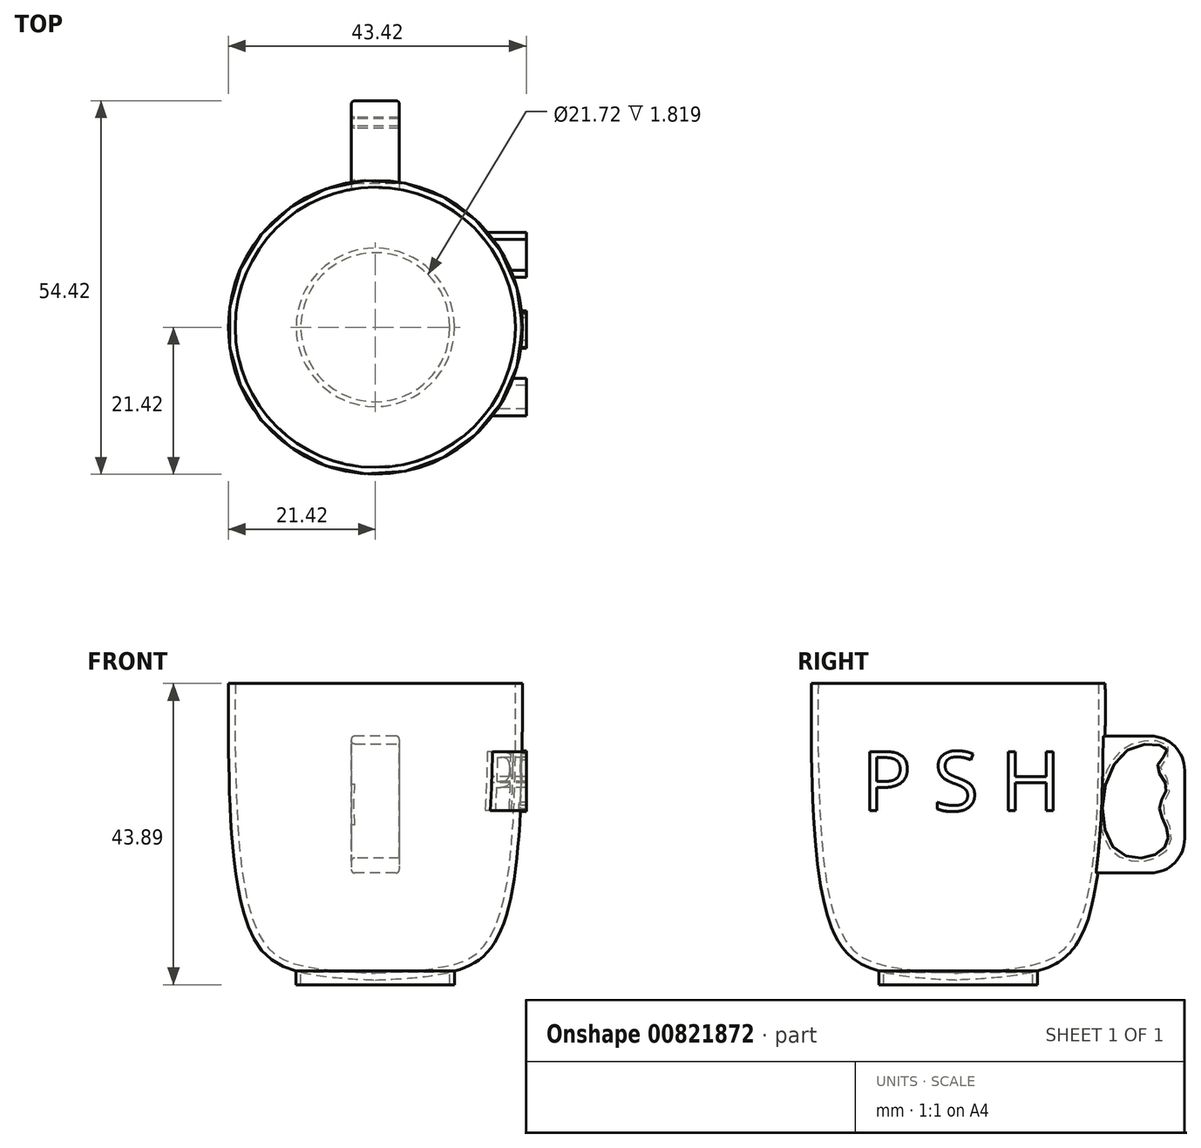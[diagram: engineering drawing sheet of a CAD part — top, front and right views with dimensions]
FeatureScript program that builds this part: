
annotation { "Feature Type Name" : "Feature", "Feature Type Description" : "" }
export const myFeature = defineFeature(function(context is Context, id is Id, definition is map)
    precondition{}
    {
        {
            var Q0;
            Q0=qCreatedBy(makeId("Front.planeOp"),FACE);
            var sketch = newSketch(context, id + "F0", { "sketchPlane" : qUnion([Q0])});
            skFitSpline(sketch, "E0", {"points": [v(-1.95, -31.25) * mm, v(9.5, -30.33) * mm, v(17.51, -25.53) * mm, v(21.4, 15) * mm], "startDerivative": vector(44.83, 1.61) * mm, "endDerivative": vector(-0.44, 101.6) * mm});
            skFitSpline(sketch, "E1.0", {"points": [v(-1.98, -30.25) * mm, v(-1.05, -30.22) * mm, v(0.82, -30.15) * mm, v(3.56, -30) * mm, v(6.23, -29.8) * mm, v(8.36, -29.52) * mm, v(10, -29.23) * mm, v(11.54, -28.88) * mm, v(13.3, -28.26) * mm, v(14.8, -27.29) * mm, v(15.87, -26.18) * mm, v(16.6, -25.15) * mm, v(17.27, -23.88) * mm, v(18.06, -21.85) * mm, v(18.87, -18.74) * mm, v(19.57, -14.26) * mm, v(20.03, -9.15) * mm, v(20.3, -3.55) * mm, v(20.45, 4.41) * mm, v(20.42, 10.76) * mm, v(20.4, 15) * mm]});
            skLineSegment(sketch, "E2", {"start": v(16.6, 12.02) * mm, "end": v(24.6, 12.02) * mm});
            skLineSegment(sketch, "E3", {"start": v(0, 35.6) * mm, "end": v(0, -44.75) * mm});
            skLineSegment(sketch, "E4", {"start": v(11.55, -29.88) * mm, "end": v(11.55, -31.87) * mm});
            skLineSegment(sketch, "E5", {"start": v(11.55, -31.87) * mm, "end": v(10.86, -31.87) * mm});
            skLineSegment(sketch, "E6", {"start": v(10.86, -31.87) * mm, "end": v(10.86, -29.88) * mm});
            skSolve(sketch);
        }
        {
            var Q0;
            {var subQ3=sQuery(id+"F0.wireOp",EDGE,"E3");var subQ5=sQuery(id+"F0.wireOp",EDGE,"E0");var subQ9=makeQuery(id+"F0.imprint","INTERSECT",VERTEX,{"derivedFrom":[subQ5,subQ3]});Q0=makeQuery(id+"F0.imprint","IMPRINT",FACE,{"disambiguationData":[TD([[makeQuery(id+"F0.imprint","IMPRINT",EDGE,{"disambiguationData":[TD([[subQ9,-1.0]])],"derivedFrom":subQ5}),1.0]])]});}
            var Q1;
            {var subQ0=sQuery(id+"F0.wireOp",EDGE,"E4");Q1=makeQuery(id+"F0.imprint","IMPRINT",FACE,{"disambiguationData":[TD([[makeQuery(id+"F0.imprint","IMPRINT",EDGE,{"derivedFrom":subQ0}),-1.0]])]});}
            var Q2;
            Q2=sQuery(id+"F0.wireOp",EDGE,"E3");
            revolve(context, id + "F1", {"surfaceOperationType" : NewSurfaceOperationType.NEW, "entities" : qUnion([Q0, Q1]), "axis" : qUnion([Q2]), "revolveType" : RevolveType.FULL});
        }
        {
            var Q0;
            Q0=qCreatedBy(makeId("Right.planeOp"),FACE);
            var sketch = newSketch(context, id + "F2", { "sketchPlane" : qUnion([Q0])});
            skText(sketch, "E7", { "text": "P S H", "fontName": "OpenSans-Regular.ttf"});
            const initialGuessF2  = {"E7": [-0.01408, -0.00652, 1, 0, 0.0087]};
            skSetInitialGuess(sketch, initialGuessF2);
            skSolve(sketch);
        }
        {
            var Q0;
            Q0 = qSketchRegion(id + "F2", true);
            extrude(context, id + "F3", {"entities" : qUnion([Q0]), "operationType" : NewBodyOperationType.ADD, "depth" : 22 * mm, "offsetDistance" : 25 * mm});
        }
        {
            var Q0;
            Q0 = qSketchRegion(id + "F2", true);
            var Q1;
            Q1=makeQuery(id+"F3.boolean.opBoolean","SPLIT",FACE,{"disambiguationData":[TD([makeQuery(id+"F1.opRevolve","SWEPT_FACE",FACE,{"disambiguationData":[OSD([sQuery(id+"F0.wireOp",EDGE,"E2")])]})])],"derivedFrom":makeQuery(id+"F1.opRevolve","SWEPT_FACE",FACE,{"disambiguationData":[OSD([sQuery(id+"F0.wireOp",EDGE,"E1.0")])]})});
            extrude(context, id + "F4", {"entities" : qUnion([Q0]), "operationType" : NewBodyOperationType.REMOVE, "endBound" : BoundingType.UP_TO_SURFACE, "depth" : 25 * mm, "endBoundEntityFace" : qUnion([Q1]), "offsetDistance" : 25 * mm});
        }
        {
            var Q0;
            Q0=qCreatedBy(makeId("Front.planeOp"),FACE);
            var sketch = newSketch(context, id + "F5", { "sketchPlane" : qUnion([Q0])});
            skLineSegment(sketch, "E8.bottom", {"start": v(3.5, 4.36) * mm, "end": v(-3.5, 4.36) * mm});
            skLineSegment(sketch, "E8.top", {"start": v(3.5, -15.58) * mm, "end": v(-3.5, -15.58) * mm});
            skLineSegment(sketch, "E8.left", {"start": v(3.5, 4.36) * mm, "end": v(3.5, -15.58) * mm});
            skLineSegment(sketch, "E8.right", {"start": v(-3.5, 4.36) * mm, "end": v(-3.5, -15.58) * mm});
            skSolve(sketch);
        }
        {
            var Q0;
            Q0 = qSketchRegion(id + "F5", true);
            extrude(context, id + "F6", {"entities" : qUnion([Q0]), "operationType" : NewBodyOperationType.ADD, "oppositeDirection" : true, "depth" : 33 * mm, "offsetDistance" : 25 * mm});
        }
        {
            var Q0;
            {var subQ1=sQuery(id+"F5.wireOp",EDGE,"E8.left");Q0=makeQuery(id+"F6.boolean.opBoolean","SPLIT",FACE,{"disambiguationData":[TD([makeQuery(id+"F1.opRevolve","SWEPT_FACE",FACE,{"disambiguationData":[OSD([sQuery(id+"F0.wireOp",EDGE,"E0")])]})])],"derivedFrom":makeQuery(id+"F6.opExtrude","SWEPT_FACE",FACE,{"disambiguationData":[OSD([subQ1])]})});}
            var sketch = newSketch(context, id + "F7", { "sketchPlane" : qUnion([Q0])});
            skFitSpline(sketch, "E9", {"points": [v(30.43, 2.35) * mm, v(29.02, 0) * mm, v(30.37, -2.93) * mm, v(29.31, -5.83) * mm, v(30.45, -9.23) * mm, v(29.41, -12.47) * mm, v(22.63, -11.9) * mm, v(24.14, 1.91) * mm, v(30.43, 2.35) * mm]});
            skSolve(sketch);
        }
        {
            var Q0;
            Q0=makeQuery(id+"F7.imprint","IMPRINT",FACE,{"disambiguationData":[TD([[makeQuery(id+"F7.imprint","IMPRINT",EDGE,{"derivedFrom":sQuery(id+"F7.wireOp",EDGE,"E9")}),-1.0]])]});
            extrude(context, id + "F8", {"entities" : qUnion([Q0]), "operationType" : NewBodyOperationType.REMOVE, "oppositeDirection" : true, "depth" : 25 * mm, "offsetDistance" : 25 * mm});
        }
        {
            var Q0;
            {var subQ0=sQuery(id+"F5.wireOp",EDGE,"E8.bottom");var subQ1=sQuery(id+"F5.wireOp",EDGE,"E8.left");Q0=makeQuery(id+"F6.boolean.opBoolean","SPLIT",EDGE,{"disambiguationData":[TD([makeQuery(id+"F1.opRevolve","SWEPT_FACE",FACE,{"disambiguationData":[OSD([sQuery(id+"F0.wireOp",EDGE,"E0")])]})])],"derivedFrom":makeQuery(id+"F6.opExtrude","SWEPT_EDGE",EDGE,{"disambiguationData":[OSD([subQ0,subQ1])]})});}
            var Q1;
            Q1=makeQuery(id+"F6.opExtrude","CAP_EDGE",EDGE,{"disambiguationData":[OSD([sQuery(id+"F5.wireOp",EDGE,"E8.left")])],"isStart":false});
            var Q2;
            {var subQ0=sQuery(id+"F5.wireOp",EDGE,"E8.left");var subQ1=sQuery(id+"F5.wireOp",EDGE,"E8.top");Q2=makeQuery(id+"F6.boolean.opBoolean","SPLIT",EDGE,{"disambiguationData":[TD([makeQuery(id+"F1.opRevolve","SWEPT_FACE",FACE,{"disambiguationData":[OSD([sQuery(id+"F0.wireOp",EDGE,"E0")])]})])],"derivedFrom":makeQuery(id+"F6.opExtrude","SWEPT_EDGE",EDGE,{"disambiguationData":[OSD([subQ1,subQ0])]})});}
            var Q3;
            {var subQ0=sQuery(id+"F5.wireOp",EDGE,"E8.bottom");var subQ1=sQuery(id+"F5.wireOp",EDGE,"E8.right");Q3=makeQuery(id+"F6.boolean.opBoolean","SPLIT",EDGE,{"disambiguationData":[TD([makeQuery(id+"F1.opRevolve","SWEPT_FACE",FACE,{"disambiguationData":[OSD([sQuery(id+"F0.wireOp",EDGE,"E0")])]})])],"derivedFrom":makeQuery(id+"F6.opExtrude","SWEPT_EDGE",EDGE,{"disambiguationData":[OSD([subQ0,subQ1])]})});}
            var Q4;
            Q4=makeQuery(id+"F6.opExtrude","CAP_EDGE",EDGE,{"disambiguationData":[OSD([sQuery(id+"F5.wireOp",EDGE,"E8.right")])],"isStart":false});
            var Q5;
            {var subQ0=sQuery(id+"F5.wireOp",EDGE,"E8.right");var subQ1=sQuery(id+"F5.wireOp",EDGE,"E8.top");Q5=makeQuery(id+"F6.boolean.opBoolean","SPLIT",EDGE,{"disambiguationData":[TD([makeQuery(id+"F1.opRevolve","SWEPT_FACE",FACE,{"disambiguationData":[OSD([sQuery(id+"F0.wireOp",EDGE,"E0")])]})])],"derivedFrom":makeQuery(id+"F6.opExtrude","SWEPT_EDGE",EDGE,{"disambiguationData":[OSD([subQ1,subQ0])]})});}
            var Q6;
            Q6=makeQuery(id+"F8.boolean.opBoolean","COPY",EDGE,{"derivedFrom":makeQuery(id+"F8.opExtrude","CAP_EDGE",EDGE,{"disambiguationData":[OSD([sQuery(id+"F7.wireOp",EDGE,"E9")])],"isStart":true})});
            var Q7;
            {var subQ1=sQuery(id+"F5.wireOp",EDGE,"E8.right");Q7=makeQuery(id+"F8.boolean.opBoolean","INTERSECT",EDGE,{"derivedFrom":[makeQuery(id+"F6.boolean.opBoolean","SPLIT",FACE,{"disambiguationData":[TD([makeQuery(id+"F1.opRevolve","SWEPT_FACE",FACE,{"disambiguationData":[OSD([sQuery(id+"F0.wireOp",EDGE,"E0")])]})])],"derivedFrom":makeQuery(id+"F6.opExtrude","SWEPT_FACE",FACE,{"disambiguationData":[OSD([subQ1])]})}),makeQuery(id+"F8.opExtrude","SWEPT_FACE",FACE,{"disambiguationData":[OSD([sQuery(id+"F7.wireOp",EDGE,"E9")])]})]});}
            fillet(context, id + "F9", {"entities" : qUnion([Q0, Q1, Q2, Q3, Q4, Q5, Q6, Q7]), "radius" : 0.5 * mm, "tangentPropagation" : true, "allowEdgeOverflow" : false});
        }
        {
            var Q0;
            Q0=makeQuery(id+"F6.opExtrude","CAP_EDGE",EDGE,{"disambiguationData":[OSD([sQuery(id+"F5.wireOp",EDGE,"E8.bottom")])],"isStart":false});
            var Q1;
            Q1=makeQuery(id+"F6.opExtrude","CAP_EDGE",EDGE,{"disambiguationData":[OSD([sQuery(id+"F5.wireOp",EDGE,"E8.top")])],"isStart":false});
            fillet(context, id + "F10", {"entities" : qUnion([Q0, Q1]), "radius" : 5 * mm, "tangentPropagation" : true, "allowEdgeOverflow" : false});
        }
        {
            var Q0;
            Q0=makeQuery(id+"F6.opExtrude","CAP_FACE",FACE,{"disambiguationData":[OSD([sQuery(id+"F5.wireOp",EDGE,"E8.bottom"),sQuery(id+"F5.wireOp",EDGE,"E8.top"),sQuery(id+"F5.wireOp",EDGE,"E8.left"),sQuery(id+"F5.wireOp",EDGE,"E8.right")])],"isStart":true});
            var Q1;
            {var subQ0=sQuery(id+"F2.wireOp",EDGE,"E7.sketch_text.stroke-51");var subQ1=sQuery(id+"F2.wireOp",EDGE,"E7.sketch_text.stroke-50");var subQ2=sQuery(id+"F2.wireOp",EDGE,"E7.sketch_text.stroke-49");var subQ3=sQuery(id+"F2.wireOp",EDGE,"E7.sketch_text.stroke-48");var subQ4=sQuery(id+"F2.wireOp",EDGE,"E7.sketch_text.stroke-47");var subQ5=sQuery(id+"F2.wireOp",EDGE,"E7.sketch_text.stroke-46");var subQ6=sQuery(id+"F2.wireOp",EDGE,"E7.sketch_text.stroke-45");var subQ7=sQuery(id+"F2.wireOp",EDGE,"E7.sketch_text.stroke-44");var subQ8=sQuery(id+"F2.wireOp",EDGE,"E7.sketch_text.stroke-43");var subQ9=sQuery(id+"F2.wireOp",EDGE,"E7.sketch_text.stroke-42");var subQ10=sQuery(id+"F2.wireOp",EDGE,"E7.sketch_text.stroke-41");var subQ11=sQuery(id+"F2.wireOp",EDGE,"E7.sketch_text.stroke-40");var subQ12=sQuery(id+"F2.wireOp",EDGE,"E7.sketch_text.stroke-39");var subQ13=sQuery(id+"F2.wireOp",EDGE,"E7.sketch_text.stroke-38");var subQ14=sQuery(id+"F2.wireOp",EDGE,"E7.sketch_text.stroke-37");var subQ15=sQuery(id+"F2.wireOp",EDGE,"E7.sketch_text.stroke-36");var subQ16=sQuery(id+"F2.wireOp",EDGE,"E7.sketch_text.stroke-35");var subQ17=sQuery(id+"F2.wireOp",EDGE,"E7.sketch_text.stroke-34");var subQ18=sQuery(id+"F2.wireOp",EDGE,"E7.sketch_text.stroke-33");var subQ19=sQuery(id+"F2.wireOp",EDGE,"E7.sketch_text.stroke-32");var subQ20=sQuery(id+"F2.wireOp",EDGE,"E7.sketch_text.stroke-31");var subQ21=sQuery(id+"F2.wireOp",EDGE,"E7.sketch_text.stroke-30");var subQ22=sQuery(id+"F2.wireOp",EDGE,"E7.sketch_text.stroke-29");var subQ23=sQuery(id+"F2.wireOp",EDGE,"E7.sketch_text.stroke-28");var subQ24=sQuery(id+"F2.wireOp",EDGE,"E7.sketch_text.stroke-27");var subQ25=sQuery(id+"F2.wireOp",EDGE,"E7.sketch_text.stroke-26");var subQ26=sQuery(id+"F2.wireOp",EDGE,"E7.sketch_text.stroke-25");var subQ27=sQuery(id+"F2.wireOp",EDGE,"E7.sketch_text.stroke-24");var subQ28=sQuery(id+"F2.wireOp",EDGE,"E7.sketch_text.stroke-23");var subQ29=sQuery(id+"F2.wireOp",EDGE,"E7.sketch_text.stroke-22");var subQ30=sQuery(id+"F2.wireOp",EDGE,"E7.sketch_text.stroke-21");var subQ31=sQuery(id+"F2.wireOp",EDGE,"E7.sketch_text.stroke-20");var subQ32=sQuery(id+"F2.wireOp",EDGE,"E7.sketch_text.stroke-19");var subQ33=sQuery(id+"F2.wireOp",EDGE,"E7.sketch_text.stroke-18");var subQ34=sQuery(id+"F2.wireOp",EDGE,"E7.sketch_text.stroke-17");var subQ35=sQuery(id+"F2.wireOp",EDGE,"E7.sketch_text.stroke-16");var subQ36=sQuery(id+"F2.wireOp",EDGE,"E7.sketch_text.stroke-15");var subQ37=sQuery(id+"F2.wireOp",EDGE,"E7.sketch_text.stroke-14");var subQ38=sQuery(id+"F2.wireOp",EDGE,"E7.sketch_text.stroke-13");var subQ39=sQuery(id+"F2.wireOp",EDGE,"E7.sketch_text.stroke-12");var subQ40=sQuery(id+"F2.wireOp",EDGE,"E7.sketch_text.stroke-11");var subQ41=sQuery(id+"F2.wireOp",EDGE,"E7.sketch_text.stroke-10");var subQ42=sQuery(id+"F2.wireOp",EDGE,"E7.sketch_text.stroke-9");var subQ43=sQuery(id+"F2.wireOp",EDGE,"E7.sketch_text.stroke-8");var subQ44=sQuery(id+"F2.wireOp",EDGE,"E7.sketch_text.stroke-7");var subQ45=sQuery(id+"F2.wireOp",EDGE,"E7.sketch_text.stroke-6");var subQ46=sQuery(id+"F2.wireOp",EDGE,"E7.sketch_text.stroke-5");var subQ47=sQuery(id+"F2.wireOp",EDGE,"E7.sketch_text.stroke-4");var subQ48=sQuery(id+"F2.wireOp",EDGE,"E7.sketch_text.stroke-3");var subQ49=sQuery(id+"F2.wireOp",EDGE,"E7.sketch_text.stroke-2");var subQ50=sQuery(id+"F2.wireOp",EDGE,"E7.sketch_text.stroke-1");var subQ51=sQuery(id+"F2.wireOp",EDGE,"E7.sketch_text.stroke-0");var subQ52=makeQuery(id+"F1.opRevolve","SWEPT_FACE",FACE,{"disambiguationData":[OSD([sQuery(id+"F0.wireOp",EDGE,"E1.0")])]});Q1=makeQuery(id+"F4.boolean.opBoolean","MERGE",FACE,{"derivedFrom":[makeQuery(id+"F3.boolean.opBoolean","SPLIT",FACE,{"disambiguationData":[TD([makeQuery(id+"F3.opExtrude","SWEPT_FACE",FACE,{"disambiguationData":[OSD([subQ43])]})])],"derivedFrom":subQ52}),makeQuery(id+"F3.boolean.opBoolean","SPLIT",FACE,{"disambiguationData":[TD([makeQuery(id+"F1.opRevolve","SWEPT_FACE",FACE,{"disambiguationData":[OSD([sQuery(id+"F0.wireOp",EDGE,"E2")])]})])],"derivedFrom":subQ52}),makeQuery(id+"F4.opExtrude","CAP_FACE",FACE,{"disambiguationData":[OSD([subQ51,subQ50,subQ49,subQ48,subQ47,subQ46,subQ45,subQ44,subQ43,subQ42,subQ41,subQ40,subQ39,subQ38,subQ37])],"isStart":false}),makeQuery(id+"F4.opExtrude","CAP_FACE",FACE,{"disambiguationData":[OSD([subQ36,subQ35,subQ34,subQ33,subQ32,subQ31,subQ30,subQ29,subQ28,subQ27,subQ26,subQ25,subQ24,subQ23,subQ22,subQ21,subQ20,subQ19,subQ18,subQ17,subQ16,subQ15,subQ14,subQ13,subQ12])],"isStart":false}),makeQuery(id+"F4.opExtrude","CAP_FACE",FACE,{"disambiguationData":[OSD([subQ11,subQ10,subQ9,subQ8,subQ7,subQ6,subQ5,subQ4,subQ3,subQ2,subQ1,subQ0])],"isStart":false})]});}
            extrude(context, id + "F11", {"entities" : qUnion([Q0]), "operationType" : NewBodyOperationType.REMOVE, "endBound" : BoundingType.UP_TO_SURFACE, "oppositeDirection" : true, "depth" : 25 * mm, "endBoundEntityFace" : qUnion([Q1]), "offsetDistance" : 25 * mm});
        }
    });
